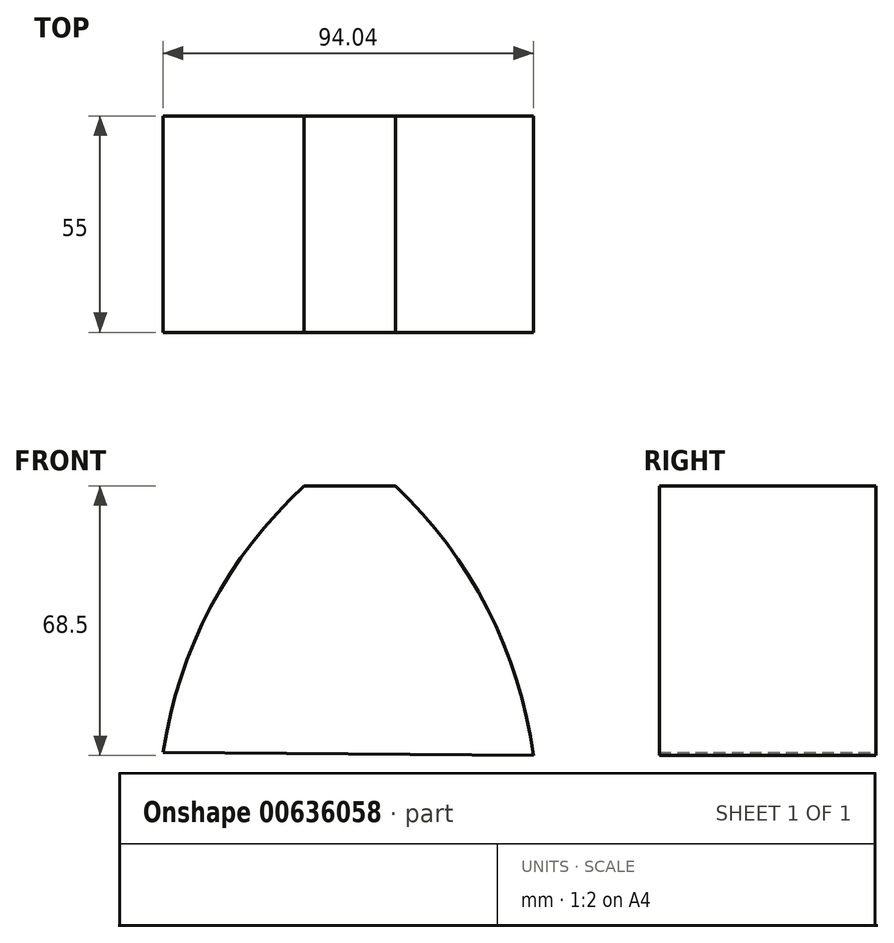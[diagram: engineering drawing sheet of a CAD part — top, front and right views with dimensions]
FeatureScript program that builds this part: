
annotation { "Feature Type Name" : "Feature", "Feature Type Description" : "" }
export const myFeature = defineFeature(function(context is Context, id is Id, definition is map)
    precondition{}
    {
        {
            var Q0;
            Q0=qCreatedBy(makeId("Front.planeOp"),FACE);
            var sketch = newSketch(context, id + "F0", { "sketchPlane" : qUnion([Q0])});
            skArc(sketch, "E0", {"start": v(35.83, 67.85) * mm, "mid": v(12.07, 37.01) * mm, "end": v(0, 0) * mm});
            skLineSegment(sketch, "E1", {"start": v(35.83, 67.85) * mm, "end": v(59, 67.85) * mm});
            skPoint(sketch, "E2.endSnap0", {"position": v(47.03, 67.85) * mm});
            skLineSegment(sketch, "E3", {"start": v(-0.34, 0.16) * mm, "end": v(94.06, -0.65) * mm});
            skPoint(sketch, "E2.end.orphan", {"position": v(47.03, 0) * mm});
            skPoint(sketch, "E4.orphan", {"position": v(58.24, 67.85) * mm});
            skArc(sketch, "E5.converted", {"start": v(59, 67.85) * mm, "mid": v(82.45, 36.63) * mm, "end": v(94.06, -0.65) * mm});
            skSolve(sketch);
        }
        {
            var Q0;
            {var subQ0=sQuery(id+"F0.wireOp",EDGE,"E1");Q0=makeQuery(id+"F0.imprint","IMPRINT",FACE,{"disambiguationData":[TD([[makeQuery(id+"F0.imprint","IMPRINT",EDGE,{"derivedFrom":subQ0}),-1.0]])]});}
            extrude(context, id + "F1", {"entities" : qUnion([Q0]), "depth" : 55 * mm, "offsetDistance" : 25.4 * mm});
        }
    });
